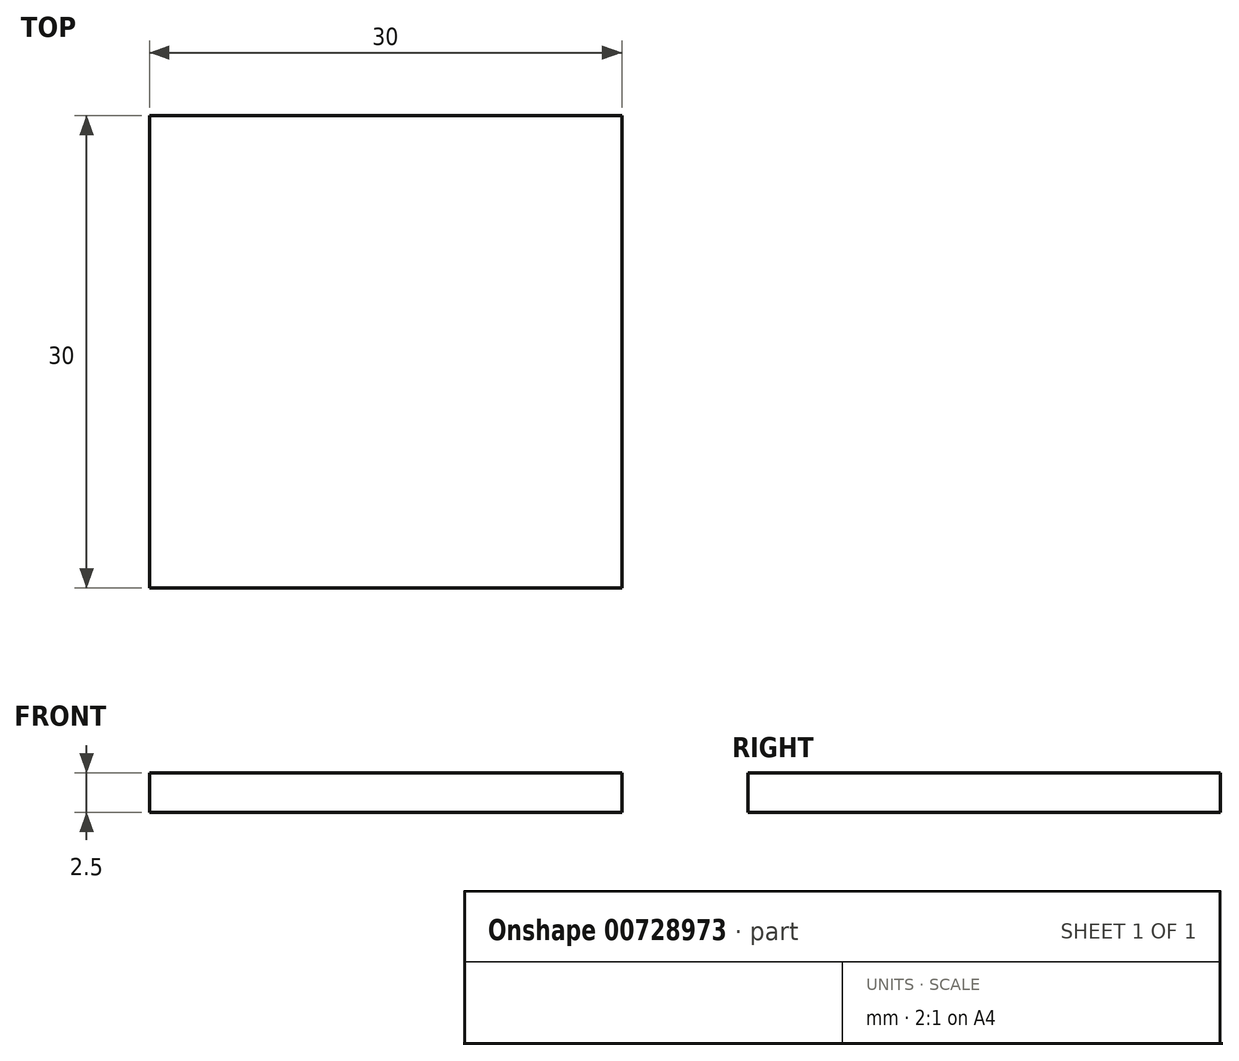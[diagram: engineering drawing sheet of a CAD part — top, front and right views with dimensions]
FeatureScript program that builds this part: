
annotation { "Feature Type Name" : "Feature", "Feature Type Description" : "" }
export const myFeature = defineFeature(function(context is Context, id is Id, definition is map)
    precondition{}
    {
        {
            var Q0;
            Q0=qCreatedBy(makeId("Top.planeOp"),FACE);
            var sketch = newSketch(context, id + "F0", { "sketchPlane" : qUnion([Q0])});
            skLineSegment(sketch, "E0.bottom", {"start": v(15, 15) * mm, "end": v(-15, 15) * mm});
            skLineSegment(sketch, "E0.top", {"start": v(15, -15) * mm, "end": v(-15, -15) * mm});
            skLineSegment(sketch, "E0.left", {"start": v(15, 15) * mm, "end": v(15, -15) * mm});
            skLineSegment(sketch, "E0.right", {"start": v(-15, 15) * mm, "end": v(-15, -15) * mm});
            skPoint(sketch, "E0.middle", {"position": v(0, 0) * mm});
            skSolve(sketch);
        }
        {
            var Q0;
            Q0=makeQuery(id+"F0.imprint","IMPRINT",FACE,{"disambiguationData":[TD([[makeQuery(id+"F0.imprint","IMPRINT",EDGE,{"derivedFrom":sQuery(id+"F0.wireOp",EDGE,"E0.bottom")}),1.0]])]});
            extrude(context, id + "F1", {"entities" : qUnion([Q0]), "depth" : 2.5 * mm, "offsetDistance" : 25.4 * mm});
        }
    });
